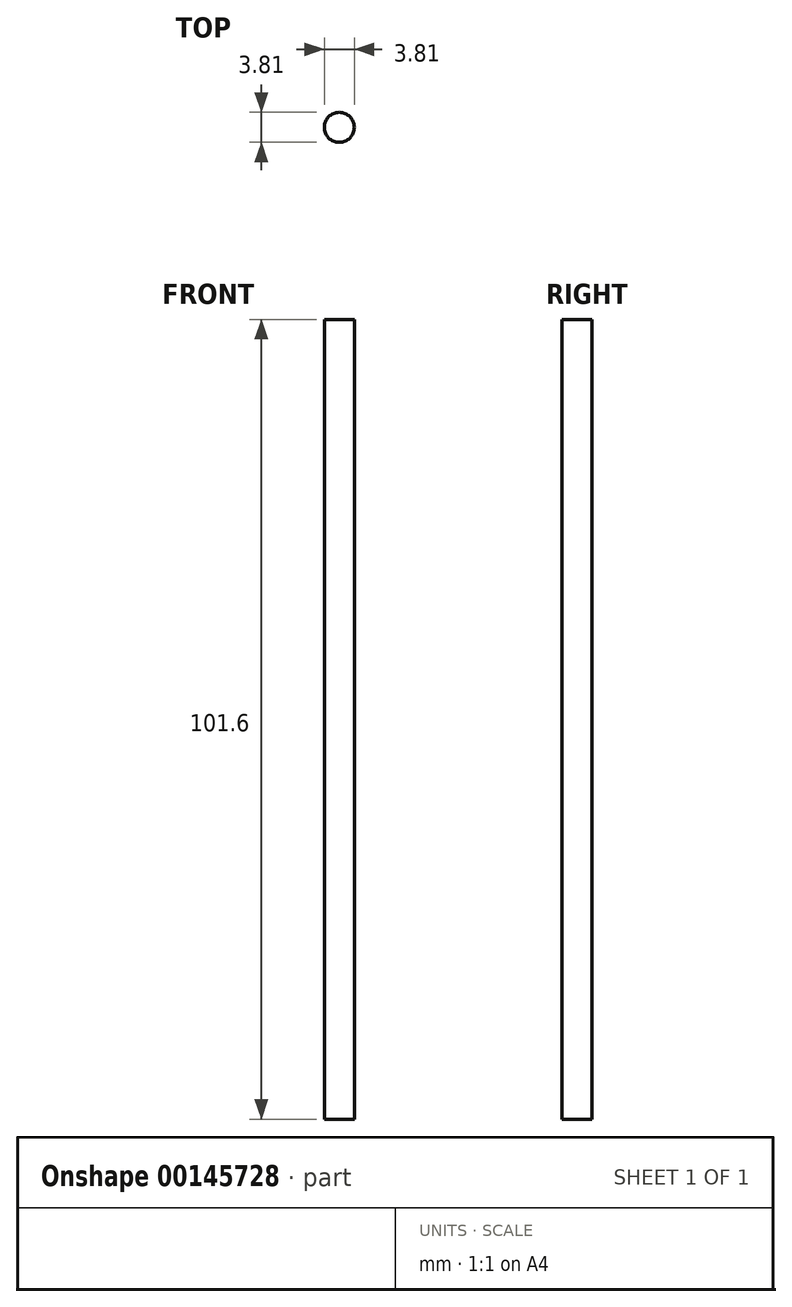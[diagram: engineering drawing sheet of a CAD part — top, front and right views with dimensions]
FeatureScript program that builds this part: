
annotation { "Feature Type Name" : "Feature", "Feature Type Description" : "" }
export const myFeature = defineFeature(function(context is Context, id is Id, definition is map)
    precondition{}
    {
        {
            var Q0;
            Q0=qCreatedBy(makeId("Top.planeOp"),FACE);
            var sketch = newSketch(context, id + "F0", { "sketchPlane" : qUnion([Q0])});
            skCircle(sketch, "E0", {"center": v(18.22, 30.06) * mm, "radius": 1.9 * mm});
            skSolve(sketch);
        }
        {
            var Q0;
            Q0=makeQuery(id+"F0.imprint","IMPRINT",FACE,{"disambiguationData":[TD([[makeQuery(id+"F0.imprint","IMPRINT",EDGE,{"derivedFrom":sQuery(id+"F0.wireOp",EDGE,"E0")}),1.0]])]});
            extrude(context, id + "F1", {"entities" : qUnion([Q0]), "depth" : 101.6 * mm});
        }
    });
